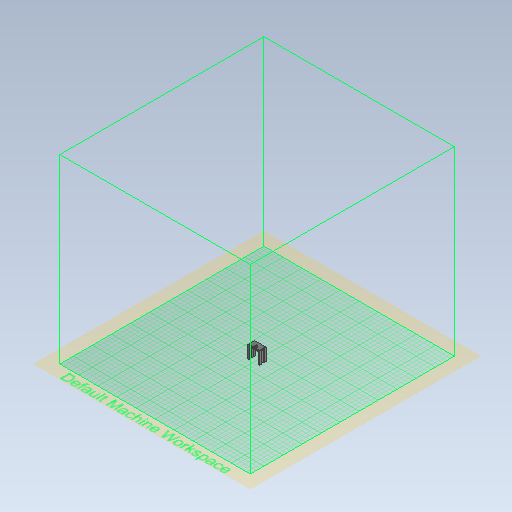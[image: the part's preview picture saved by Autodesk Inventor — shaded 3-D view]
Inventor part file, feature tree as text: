
AUTODESK INVENTOR PART (.ipt)
format: ipt  version: 2020 (Build 240168000, 168)  size: 560,128 bytes
history: native  units: mm
features: extrude x10, projected_geometry x7, sketch x5, fillet x4
ambient origin geometry x8: Origin, YZ Plane, XZ Plane, XY Plane, X Axis, Y Axis, Z Axis, Center Point
bodies: Body1 (feature_tree)
feature tree (26):
  extrude  "Выдавливание7"  Depth=4.0mm
  extrude  "Выдавливание16"  Depth=25.5mm
  sketch  "Эскиз12"
  extrude  "Выдавливание17"  Depth=3.0mm
  extrude  "Выдавливание18"  Depth=3.0mm
  extrude  "Выдавливание19"  Depth=3.0mm
  fillet  "Сопряжение1"  Radius=20.2mm
  extrude  "Выдавливание20"  Depth=14.0mm TaperAngle=0.0deg
  fillet  "Сопряжение2"  Radius=26.0mm
  extrude  "Выдавливание21"  Depth=20.5mm
  extrude  "Выдавливание22"  Depth=3.0mm
  extrude  "Выдавливание23"  Depth=1.5mm
  extrude  "Выдавливание24"  Depth=0.5mm
  fillet  "Сопряжение3"  Radius=0.5mm
  fillet  "Сопряжение4"  Radius=0.5mm
  sketch  "Эскиз1"
  sketch  "Эскиз10"
  projected_geometry  "Спроецированная петля9"
  projected_geometry  "Спроецированная петля10"
  projected_geometry  "Спроецированная петля11"
  projected_geometry  "Спроецированная петля12"
  projected_geometry  "Спроецированная петля13"
  sketch  "Эскиз14"
  projected_geometry  "Спроецированная петля15"
  sketch  "Эскиз16"
  projected_geometry  "Спроецированная петля16"
